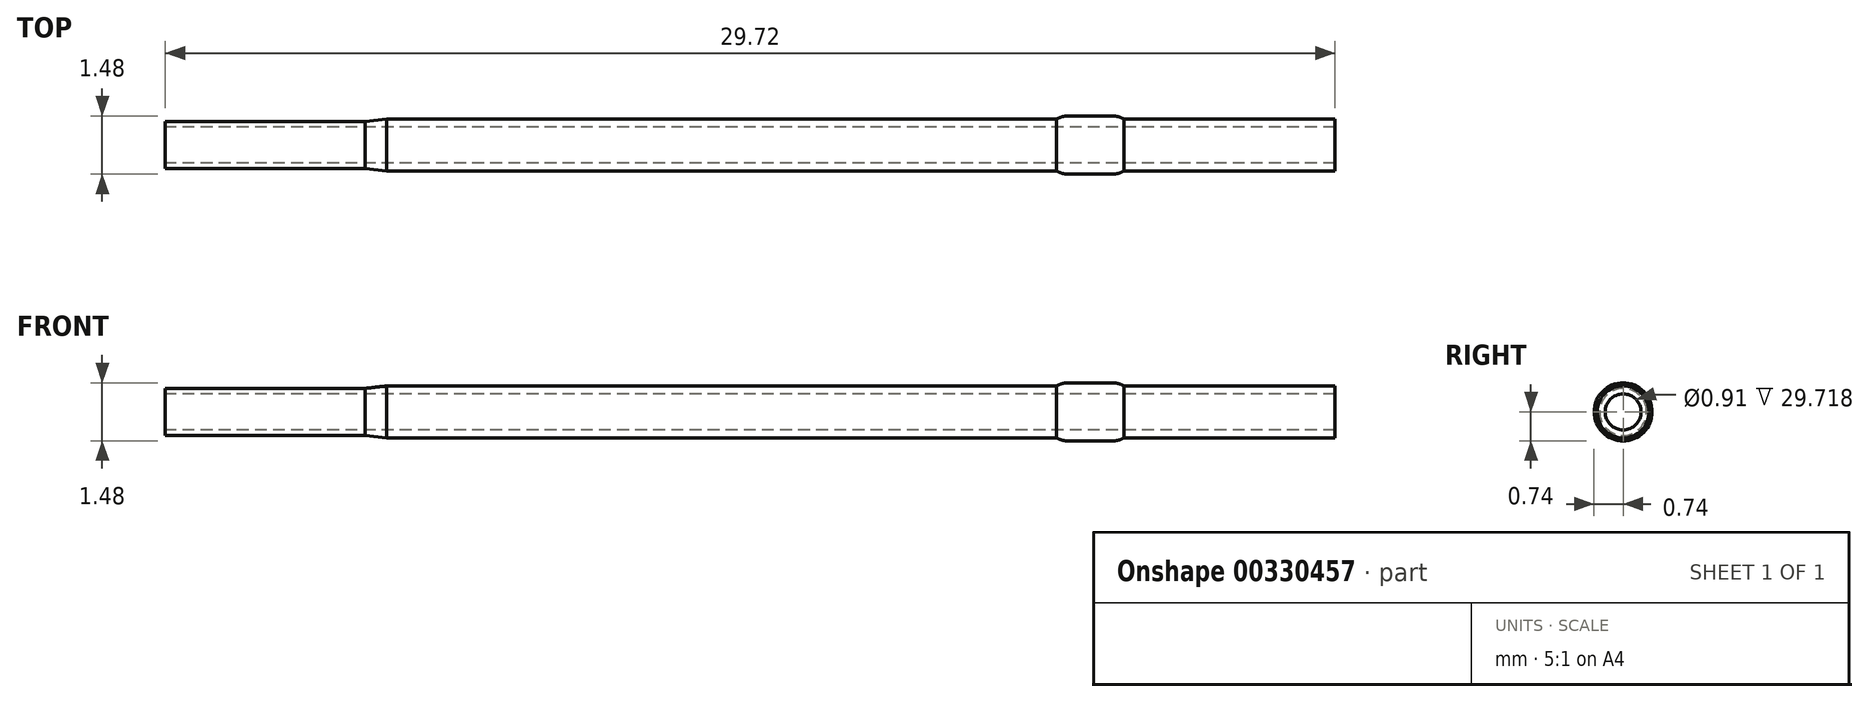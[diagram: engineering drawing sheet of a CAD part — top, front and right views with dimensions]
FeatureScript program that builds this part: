
annotation { "Feature Type Name" : "Feature", "Feature Type Description" : "" }
export const myFeature = defineFeature(function(context is Context, id is Id, definition is map)
    precondition{}
    {
        {
            var Q0;
            Q0=qCreatedBy(makeId("Front.planeOp"),FACE);
            var sketch = newSketch(context, id + "F0", { "sketchPlane" : qUnion([Q0])});
            skLineSegment(sketch, "E0", {"start": v(0, 0) * mm, "end": v(0, 0.6) * mm});
            skLineSegment(sketch, "E1", {"start": v(0, 0) * mm, "end": v(29.72, 0) * mm});
            skLineSegment(sketch, "E2", {"start": v(0, 0.6) * mm, "end": v(5.08, 0.6) * mm});
            skLineSegment(sketch, "E3", {"start": v(5.63, 0.66) * mm, "end": v(22.64, 0.66) * mm});
            skLineSegment(sketch, "E4", {"start": v(5.08, 0.6) * mm, "end": v(5.63, 0.66) * mm});
            skLineSegment(sketch, "E5", {"start": v(5.63, 0.66) * mm, "end": v(5.63, 0) * mm});
            skLineSegment(sketch, "E6", {"start": v(5.08, 0.6) * mm, "end": v(5.08, 0) * mm});
            skLineSegment(sketch, "E7", {"start": v(29.72, 0) * mm, "end": v(29.72, 0.66) * mm});
            skLineSegment(sketch, "E8", {"start": v(22.64, 0.74) * mm, "end": v(24.35, 0.74) * mm});
            skLineSegment(sketch, "E9", {"start": v(22.64, 0.74) * mm, "end": v(22.64, 0.66) * mm});
            skLineSegment(sketch, "E10", {"start": v(29.72, 0.66) * mm, "end": v(24.35, 0.66) * mm});
            skLineSegment(sketch, "E11", {"start": v(24.35, 0.66) * mm, "end": v(24.35, 0.74) * mm});
            skSolve(sketch);
        }
        {
            var Q0;
            {var subQ0=sQuery(id+"F0.wireOp",EDGE,"E0");Q0=makeQuery(id+"F0.imprint","IMPRINT",FACE,{"disambiguationData":[TD([[makeQuery(id+"F0.imprint","IMPRINT",EDGE,{"derivedFrom":subQ0}),-1.0]])]});}
            var Q1;
            Q1=makeQuery(id+"F0.imprint","IMPRINT",FACE,{"disambiguationData":[TD([[makeQuery(id+"F0.imprint","IMPRINT",EDGE,{"derivedFrom":sQuery(id+"F0.wireOp",EDGE,"E3")}),-1.0]])]});
            var Q2;
            Q2=makeQuery(id+"F0.imprint","IMPRINT",FACE,{"disambiguationData":[TD([[makeQuery(id+"F0.imprint","IMPRINT",EDGE,{"derivedFrom":sQuery(id+"F0.wireOp",EDGE,"E4")}),-1.0]])]});
            var Q3;
            Q3=sQuery(id+"F0.wireOp",EDGE,"E1");
            revolve(context, id + "F1", {"entities" : qUnion([Q0, Q1, Q2]), "axis" : qUnion([Q3]), "revolveType" : RevolveType.FULL});
        }
        {
            var Q0;
            Q0=qCreatedBy(makeId("Right.planeOp"),FACE);
            var sketch = newSketch(context, id + "F2", { "sketchPlane" : qUnion([Q0])});
            skCircle(sketch, "E12", {"center": v(0, 0) * mm, "radius": 0.46 * mm});
            skSolve(sketch);
        }
        {
            var Q0;
            Q0=sQuery(id+"F2.wireOp",VERTEX,"E12.center");
            var Q1;
            Q1=makeQuery(id+"F1.opRevolve","SWEPT_BODY",BODY,{"disambiguationData":[OSD([sQuery(id+"F0.wireOp",EDGE,"E0"),sQuery(id+"F0.wireOp",EDGE,"E1"),sQuery(id+"F0.wireOp",EDGE,"E2"),sQuery(id+"F0.wireOp",EDGE,"E3"),sQuery(id+"F0.wireOp",EDGE,"E4"),sQuery(id+"F0.wireOp",EDGE,"E7"),sQuery(id+"F0.wireOp",EDGE,"E8"),sQuery(id+"F0.wireOp",EDGE,"E9"),sQuery(id+"F0.wireOp",EDGE,"E10"),sQuery(id+"F0.wireOp",EDGE,"E11")])]});
            hole(context, id + "F3", {"style" : HoleStyle.SIMPLE, "endStyle" : HoleEndStyle.THROUGH, "oppositeDirection" : true, "holeDiameter" : 0.91 * mm, "tappedDepth" : 12.7 * mm, "tapClearance" : 3, "locations" : qUnion([Q0]), "scope" : qUnion([Q1])});
        }
        {
            var Q0;
            Q0=makeQuery(id+"F1.opRevolve","SWEPT_EDGE",EDGE,{"disambiguationData":[OSD([sQuery(id+"F0.wireOp",EDGE,"E8"),sQuery(id+"F0.wireOp",EDGE,"E11")])]});
            fillet(context, id + "F4", {"entities" : qUnion([Q0]), "radius" : 0.56 * mm, "allowEdgeOverflow" : false});
        }
        {
            var Q0;
            Q0=makeQuery(id+"F1.opRevolve","SWEPT_EDGE",EDGE,{"disambiguationData":[OSD([sQuery(id+"F0.wireOp",EDGE,"E8"),sQuery(id+"F0.wireOp",EDGE,"E9")])]});
            fillet(context, id + "F5", {"entities" : qUnion([Q0]), "radius" : 0.56 * mm, "allowEdgeOverflow" : false});
        }
    });
